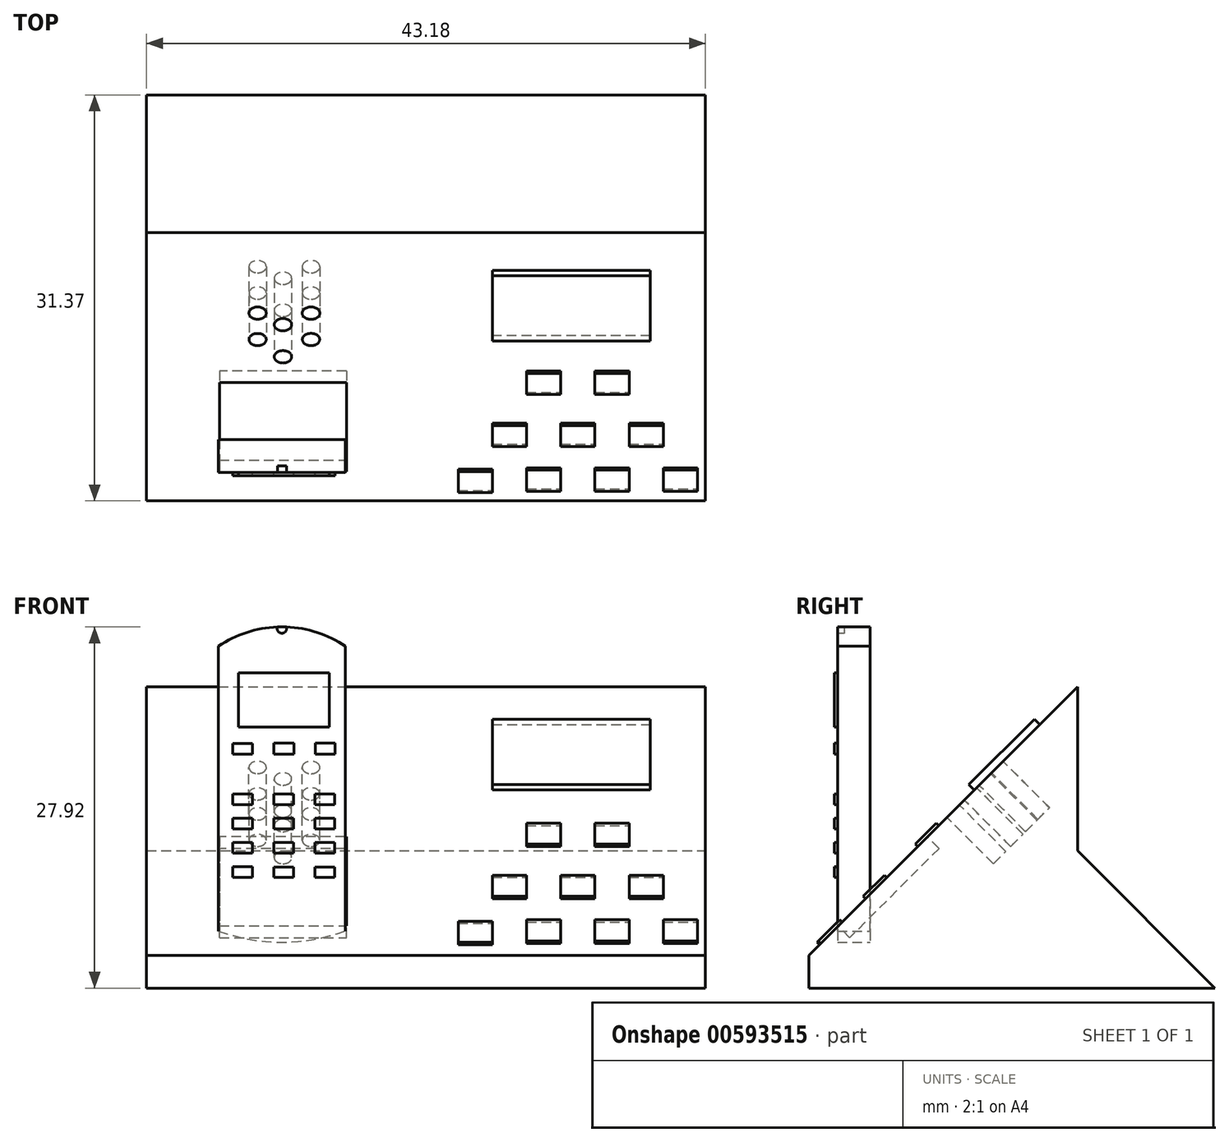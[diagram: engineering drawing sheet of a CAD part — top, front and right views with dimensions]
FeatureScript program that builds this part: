
annotation { "Feature Type Name" : "Feature", "Feature Type Description" : "" }
export const myFeature = defineFeature(function(context is Context, id is Id, definition is map)
    precondition{}
    {
        {
            var Q0;
            Q0=qCreatedBy(makeId("Top.planeOp"),FACE);
            var sketch = newSketch(context, id + "F0", { "sketchPlane" : qUnion([Q0])});
            skLineSegment(sketch, "E0", {"start": v(-21.03, 15.25) * mm, "end": v(22.15, 15.25) * mm});
            skLineSegment(sketch, "E1", {"start": v(-21.03, 15.25) * mm, "end": v(-21.03, -16.12) * mm});
            skLineSegment(sketch, "E2", {"start": v(-21.03, -16.12) * mm, "end": v(22.15, -16.12) * mm});
            skLineSegment(sketch, "E3", {"start": v(22.15, -16.12) * mm, "end": v(22.15, 15.25) * mm});
            skLineSegment(sketch, "E4", {"start": v(-21.03, 4.62) * mm, "end": v(22.15, 4.62) * mm});
            skSolve(sketch);
        }
        {
            var Q0;
            {var subQ0=sQuery(id+"F0.wireOp",EDGE,"E2");Q0=makeQuery(id+"F0.imprint","IMPRINT",FACE,{"disambiguationData":[TD([[makeQuery(id+"F0.imprint","IMPRINT",EDGE,{"derivedFrom":subQ0}),1.0]])]});}
            extrude(context, id + "F1", {"entities" : qUnion([Q0]), "depth" : 25.4 * mm, "offsetDistance" : 25.4 * mm});
        }
        {
            var Q0;
            {var subQ0=sQuery(id+"F0.wireOp",EDGE,"E0");Q0=makeQuery(id+"F0.imprint","IMPRINT",FACE,{"disambiguationData":[TD([[makeQuery(id+"F0.imprint","IMPRINT",EDGE,{"derivedFrom":subQ0}),-1.0]])]});}
            extrude(context, id + "F2", {"entities" : qUnion([Q0]), "operationType" : NewBodyOperationType.ADD, "depth" : 12.7 * mm, "offsetDistance" : 25.4 * mm});
        }
        {
            var Q0;
            Q0=makeQuery(id+"F1.opExtrude","CAP_EDGE",EDGE,{"disambiguationData":[OSD([sQuery(id+"F0.wireOp",EDGE,"E2")])],"isStart":false});
            chamfer(context, id + "F3", {"entities" : qUnion([Q0]), "width" : 22.86 * mm, "tangentPropagation" : true});
        }
        {
            var Q0;
            Q0=makeQuery(id+"F2.opExtrude","CAP_EDGE",EDGE,{"disambiguationData":[OSD([sQuery(id+"F0.wireOp",EDGE,"E0")])],"isStart":false});
            chamfer(context, id + "F4", {"entities" : qUnion([Q0]), "width" : 12.7 * mm, "tangentPropagation" : true});
        }
        {
            var Q0;
            Q0=makeQuery(id+"F3.opChamfer","BLEND_FACE",FACE,{"disambiguationData":[OSD([sQuery(id+"F0.wireOp",EDGE,"E2")])]});
            var sketch = newSketch(context, id + "F5", { "sketchPlane" : qUnion([Q0])});
            skLineSegment(sketch, "E5", {"start": v(-15.4, -6.41) * mm, "end": v(-5.59, -6.41) * mm});
            skLineSegment(sketch, "E6", {"start": v(-5.59, 3.34) * mm, "end": v(-15.4, 3.34) * mm});
            skLineSegment(sketch, "E7", {"start": v(-15.4, 3.34) * mm, "end": v(-15.4, -6.41) * mm});
            skLineSegment(sketch, "E8", {"start": v(-5.59, 3.34) * mm, "end": v(-5.59, -6.41) * mm});
            skSolve(sketch);
        }
        {
            var Q0;
            Q0=makeQuery(id+"F5.imprint","IMPRINT",FACE,{"disambiguationData":[TD([[makeQuery(id+"F5.imprint","IMPRINT",EDGE,{"derivedFrom":sQuery(id+"F5.wireOp",EDGE,"E5")}),1.0]])]});
            var Q1;
            {var subQ0=sQuery(id+"F5.wireOp",EDGE,"CrR3xn1p-6xJD-kxk5-ltNI-Yj6EOk7hMHrn");Q1=makeQuery(id+"F5.imprint","IMPRINT",FACE,{"disambiguationData":[TD([[makeQuery(id+"F5.imprint","IMPRINT",EDGE,{"derivedFrom":subQ0}),1.0]])]});}
            extrude(context, id + "F6", {"entities" : qUnion([Q0, Q1]), "operationType" : NewBodyOperationType.REMOVE, "oppositeDirection" : true, "depth" : 1.27 * mm, "offsetDistance" : 25.4 * mm});
        }
        {
            var Q0;
            {var subQ5=sQuery(id+"F5.wireOp",EDGE,"E5");Q0=makeQuery(id+"F5.imprint","IMPRINT",FACE,{"disambiguationData":[TD([[makeQuery(id+"F5.imprint","IMPRINT",EDGE,{"derivedFrom":subQ5}),-1.0]])]});}
            var sketch = newSketch(context, id + "F7", { "sketchPlane" : qUnion([Q0])});
            skLineSegment(sketch, "E9", {"start": v(5.69, 15.6) * mm, "end": v(17.9, 15.6) * mm});
            skLineSegment(sketch, "E10", {"start": v(17.9, 15.6) * mm, "end": v(17.9, 8.46) * mm});
            skLineSegment(sketch, "E11", {"start": v(17.9, 8.46) * mm, "end": v(5.69, 8.46) * mm});
            skLineSegment(sketch, "E12", {"start": v(5.69, 8.46) * mm, "end": v(5.69, 15.6) * mm});
            skLineSegment(sketch, "E13.bottom", {"start": v(8.32, 4.58) * mm, "end": v(10.97, 4.58) * mm});
            skLineSegment(sketch, "E13.top", {"start": v(8.32, 2.27) * mm, "end": v(10.97, 2.27) * mm});
            skLineSegment(sketch, "E13.left", {"start": v(8.32, 4.58) * mm, "end": v(8.32, 2.27) * mm});
            skLineSegment(sketch, "E13.right", {"start": v(10.97, 4.58) * mm, "end": v(10.97, 2.27) * mm});
            skLineSegment(sketch, "E14.bottom", {"start": v(13.61, 4.58) * mm, "end": v(16.25, 4.58) * mm});
            skLineSegment(sketch, "E14.top", {"start": v(13.61, 2.27) * mm, "end": v(16.25, 2.27) * mm});
            skLineSegment(sketch, "E14.left", {"start": v(13.61, 4.58) * mm, "end": v(13.61, 2.27) * mm});
            skLineSegment(sketch, "E14.right", {"start": v(16.25, 4.58) * mm, "end": v(16.25, 2.27) * mm});
            skLineSegment(sketch, "E15.bottom", {"start": v(5.69, -1.1) * mm, "end": v(8.33, -1.1) * mm});
            skLineSegment(sketch, "E15.top", {"start": v(5.69, -3.41) * mm, "end": v(8.33, -3.41) * mm});
            skLineSegment(sketch, "E15.left", {"start": v(5.69, -1.1) * mm, "end": v(5.69, -3.41) * mm});
            skLineSegment(sketch, "E15.right", {"start": v(8.33, -1.1) * mm, "end": v(8.33, -3.41) * mm});
            skLineSegment(sketch, "E16.bottom", {"start": v(10.97, -3.41) * mm, "end": v(13.61, -3.41) * mm});
            skLineSegment(sketch, "E16.top", {"start": v(10.97, -1.1) * mm, "end": v(13.61, -1.1) * mm});
            skLineSegment(sketch, "E16.left", {"start": v(10.97, -3.41) * mm, "end": v(10.97, -1.1) * mm});
            skLineSegment(sketch, "E16.right", {"start": v(13.61, -3.41) * mm, "end": v(13.61, -1.1) * mm});
            skLineSegment(sketch, "E17.bottom", {"start": v(16.25, -1.1) * mm, "end": v(18.9, -1.1) * mm});
            skLineSegment(sketch, "E17.top", {"start": v(16.25, -3.41) * mm, "end": v(18.9, -3.41) * mm});
            skLineSegment(sketch, "E17.left", {"start": v(16.25, -1.1) * mm, "end": v(16.25, -3.41) * mm});
            skLineSegment(sketch, "E17.right", {"start": v(18.9, -1.1) * mm, "end": v(18.9, -3.41) * mm});
            skPoint(sketch, "E18.oppositeSnap0", {"position": v(5.69, -2.26) * mm});
            skLineSegment(sketch, "E18.bottom", {"start": v(3.04, -6.14) * mm, "end": v(5.69, -6.14) * mm});
            skLineSegment(sketch, "E18.top", {"start": v(3.04, -8.45) * mm, "end": v(5.69, -8.45) * mm});
            skLineSegment(sketch, "E18.left", {"start": v(3.04, -6.14) * mm, "end": v(3.04, -8.45) * mm});
            skLineSegment(sketch, "E18.right", {"start": v(5.69, -6.14) * mm, "end": v(5.69, -8.45) * mm});
            skLineSegment(sketch, "E19.bottom", {"start": v(8.33, -6) * mm, "end": v(10.97, -6) * mm});
            skLineSegment(sketch, "E19.top", {"start": v(8.33, -8.3) * mm, "end": v(10.97, -8.3) * mm});
            skLineSegment(sketch, "E19.left", {"start": v(8.33, -6) * mm, "end": v(8.33, -8.3) * mm});
            skLineSegment(sketch, "E19.right", {"start": v(10.97, -6) * mm, "end": v(10.97, -8.3) * mm});
            skLineSegment(sketch, "E20", {"start": v(13.61, -8.3) * mm, "end": v(13.61, -6) * mm});
            skLineSegment(sketch, "E21", {"start": v(13.61, -6) * mm, "end": v(16.25, -6) * mm});
            skLineSegment(sketch, "E22", {"start": v(13.61, -8.3) * mm, "end": v(16.25, -8.3) * mm});
            skLineSegment(sketch, "E23", {"start": v(16.25, -8.3) * mm, "end": v(16.25, -6) * mm});
            skLineSegment(sketch, "E24", {"start": v(18.9, -8.3) * mm, "end": v(18.9, -6) * mm});
            skLineSegment(sketch, "E25", {"start": v(18.9, -6) * mm, "end": v(21.54, -6) * mm});
            skLineSegment(sketch, "E26", {"start": v(18.9, -8.3) * mm, "end": v(21.54, -8.3) * mm});
            skLineSegment(sketch, "E27", {"start": v(21.54, -8.3) * mm, "end": v(21.54, -6) * mm});
            skSolve(sketch);
        }
        {
            var Q0;
            Q0=makeQuery(id+"F7.imprint","IMPRINT",FACE,{"disambiguationData":[TD([[makeQuery(id+"F7.imprint","IMPRINT",EDGE,{"derivedFrom":sQuery(id+"F7.wireOp",EDGE,"E13.bottom")}),-1.0]])]});
            var Q1;
            Q1=makeQuery(id+"F7.imprint","IMPRINT",FACE,{"disambiguationData":[TD([[makeQuery(id+"F7.imprint","IMPRINT",EDGE,{"derivedFrom":sQuery(id+"F7.wireOp",EDGE,"E14.bottom")}),-1.0]])]});
            var Q2;
            Q2=makeQuery(id+"F7.imprint","IMPRINT",FACE,{"disambiguationData":[TD([[makeQuery(id+"F7.imprint","IMPRINT",EDGE,{"derivedFrom":sQuery(id+"F7.wireOp",EDGE,"E15.bottom")}),-1.0]])]});
            var Q3;
            Q3=makeQuery(id+"F7.imprint","IMPRINT",FACE,{"disambiguationData":[TD([[makeQuery(id+"F7.imprint","IMPRINT",EDGE,{"derivedFrom":sQuery(id+"F7.wireOp",EDGE,"E16.bottom")}),1.0]])]});
            var Q4;
            Q4=makeQuery(id+"F7.imprint","IMPRINT",FACE,{"disambiguationData":[TD([[makeQuery(id+"F7.imprint","IMPRINT",EDGE,{"derivedFrom":sQuery(id+"F7.wireOp",EDGE,"E17.bottom")}),-1.0]])]});
            var Q5;
            Q5=makeQuery(id+"F7.imprint","IMPRINT",FACE,{"disambiguationData":[TD([[makeQuery(id+"F7.imprint","IMPRINT",EDGE,{"derivedFrom":sQuery(id+"F7.wireOp",EDGE,"E18.bottom")}),-1.0]])]});
            var Q6;
            Q6=makeQuery(id+"F7.imprint","IMPRINT",FACE,{"disambiguationData":[TD([[makeQuery(id+"F7.imprint","IMPRINT",EDGE,{"derivedFrom":sQuery(id+"F7.wireOp",EDGE,"E19.bottom")}),-1.0]])]});
            var Q7;
            Q7=makeQuery(id+"F7.imprint","IMPRINT",FACE,{"disambiguationData":[TD([[makeQuery(id+"F7.imprint","IMPRINT",EDGE,{"derivedFrom":sQuery(id+"F7.wireOp",EDGE,"n9DK5ZvR-02UD-aitn-EGnA-fwqdZmRXGBVk.bottom")}),-1.0]])]});
            var Q8;
            Q8=makeQuery(id+"F7.imprint","IMPRINT",FACE,{"disambiguationData":[TD([[makeQuery(id+"F7.imprint","IMPRINT",EDGE,{"derivedFrom":sQuery(id+"F7.wireOp",EDGE,"2ktXjHqj-TVGW-xtYU-XM9Q-utSsLYBZR9na.bottom")}),-1.0]])]});
            var Q9;
            Q9=makeQuery(id+"F7.imprint","IMPRINT",FACE,{"disambiguationData":[TD([[makeQuery(id+"F7.imprint","IMPRINT",EDGE,{"derivedFrom":sQuery(id+"F7.wireOp",EDGE,"E20")}),-1.0]])]});
            var Q10;
            Q10=makeQuery(id+"F7.imprint","IMPRINT",FACE,{"disambiguationData":[TD([[makeQuery(id+"F7.imprint","IMPRINT",EDGE,{"derivedFrom":sQuery(id+"F7.wireOp",EDGE,"E24")}),-1.0]])]});
            extrude(context, id + "F8", {"entities" : qUnion([Q0, Q1, Q2, Q3, Q4, Q5, Q6, Q7, Q8, Q9, Q10]), "operationType" : NewBodyOperationType.ADD, "depth" : 0.25 * mm, "offsetDistance" : 25.4 * mm});
        }
        {
            var Q0;
            Q0=makeQuery(id+"F7.imprint","IMPRINT",FACE,{"disambiguationData":[TD([[makeQuery(id+"F7.imprint","IMPRINT",EDGE,{"derivedFrom":sQuery(id+"F7.wireOp",EDGE,"E9")}),-1.0]])]});
            extrude(context, id + "F9", {"entities" : qUnion([Q0]), "operationType" : NewBodyOperationType.ADD, "depth" : 0.58 * mm, "offsetDistance" : 25.4 * mm});
        }
        {
            var Q0;
            Q0=qCreatedBy(makeId("Front.planeOp"),FACE);
            var sketch = newSketch(context, id + "F10", { "sketchPlane" : qUnion([Q0])});
            skLineSegment(sketch, "E28", {"start": v(40.13, 22.63) * mm, "end": v(40.13, 0.6) * mm});
            skLineSegment(sketch, "E29", {"start": v(49.93, 0.6) * mm, "end": v(49.93, 22.63) * mm});
            skArc(sketch, "E30", {"start": v(49.93, 22.63) * mm, "mid": v(45.03, 24.11) * mm, "end": v(40.13, 22.63) * mm});
            skArc(sketch, "E31", {"start": v(40.13, 0.6) * mm, "mid": v(45.03, -0.26) * mm, "end": v(49.93, 0.6) * mm});
            skSolve(sketch);
        }
        {
            var Q0;
            Q0=makeQuery(id+"F10.imprint","IMPRINT",FACE,{"disambiguationData":[TD([[makeQuery(id+"F10.imprint","IMPRINT",EDGE,{"derivedFrom":sQuery(id+"F10.wireOp",EDGE,"E28")}),1.0]])]});
            extrude(context, id + "F11", {"entities" : qUnion([Q0]), "depth" : 2.54 * mm, "offsetDistance" : 25.4 * mm});
        }
        {
            var Q0;
            Q0=makeQuery(id+"F11.opExtrude","SWEPT_BODY",BODY,{"disambiguationData":[OSD([sQuery(id+"F10.wireOp",EDGE,"E28"),sQuery(id+"F10.wireOp",EDGE,"E29"),sQuery(id+"F10.wireOp",EDGE,"E30"),sQuery(id+"F10.wireOp",EDGE,"E31")])]});
            transform(context, id + "F12", {"entities" : qUnion([Q0]), "transformType" : TransformType.TRANSLATION_3D, "dx" : -55.6 * mm, "dy" : -11.38 * mm, "dz" : 3.81 * mm, "makeCopy" : false});
        }
        {
            var Q0;
            Q0=makeQuery(id+"F11.opExtrude","CAP_FACE",FACE,{"disambiguationData":[OSD([sQuery(id+"F10.wireOp",EDGE,"E28"),sQuery(id+"F10.wireOp",EDGE,"E29"),sQuery(id+"F10.wireOp",EDGE,"E30"),sQuery(id+"F10.wireOp",EDGE,"E31")])],"isStart":false});
            var sketch = newSketch(context, id + "F13", { "sketchPlane" : qUnion([Q0])});
            skPoint(sketch, "E32.cCircle.centerSnap0", {"position": v(-10.57, 27.92) * mm});
            skCircle(sketch, "E33", {"center": v(-10.57, 27.8) * mm, "radius": 0.37 * mm});
            skLineSegment(sketch, "E34.bottom", {"start": v(-13.94, 24.36) * mm, "end": v(-6.9, 24.36) * mm});
            skLineSegment(sketch, "E34.top", {"start": v(-13.94, 20.19) * mm, "end": v(-6.9, 20.19) * mm});
            skLineSegment(sketch, "E34.left", {"start": v(-13.94, 24.36) * mm, "end": v(-13.94, 20.19) * mm});
            skLineSegment(sketch, "E34.right", {"start": v(-6.9, 24.36) * mm, "end": v(-6.9, 20.19) * mm});
            skPoint(sketch, "E35.centerSnap0", {"position": v(-10.42, 20.19) * mm});
            skLineSegment(sketch, "E36.bottom", {"start": v(-14.36, 18.9) * mm, "end": v(-12.83, 18.9) * mm});
            skLineSegment(sketch, "E36.top", {"start": v(-14.36, 18.1) * mm, "end": v(-12.83, 18.1) * mm});
            skLineSegment(sketch, "E36.left", {"start": v(-14.36, 18.9) * mm, "end": v(-14.36, 18.1) * mm});
            skLineSegment(sketch, "E36.right", {"start": v(-12.83, 18.9) * mm, "end": v(-12.83, 18.1) * mm});
            skLineSegment(sketch, "E37.bottom", {"start": v(-11.18, 18.93) * mm, "end": v(-9.65, 18.93) * mm});
            skLineSegment(sketch, "E37.top", {"start": v(-11.18, 18.1) * mm, "end": v(-9.65, 18.1) * mm});
            skLineSegment(sketch, "E37.left", {"start": v(-11.18, 18.93) * mm, "end": v(-11.18, 18.1) * mm});
            skLineSegment(sketch, "E37.right", {"start": v(-9.65, 18.93) * mm, "end": v(-9.65, 18.1) * mm});
            skLineSegment(sketch, "E38.bottom", {"start": v(-8, 18.93) * mm, "end": v(-6.48, 18.93) * mm});
            skLineSegment(sketch, "E38.top", {"start": v(-8, 18.1) * mm, "end": v(-6.48, 18.1) * mm});
            skLineSegment(sketch, "E38.left", {"start": v(-8, 18.93) * mm, "end": v(-8, 18.1) * mm});
            skLineSegment(sketch, "E38.right", {"start": v(-6.48, 18.93) * mm, "end": v(-6.48, 18.1) * mm});
            skCircle(sketch, "E39", {"center": v(-10.42, 16.7) * mm, "radius": 0.91 * mm});
            skLineSegment(sketch, "E40.bottom", {"start": v(-14.36, 15) * mm, "end": v(-12.84, 15) * mm});
            skLineSegment(sketch, "E40.top", {"start": v(-14.36, 14.2) * mm, "end": v(-12.84, 14.2) * mm});
            skLineSegment(sketch, "E40.left", {"start": v(-14.36, 15) * mm, "end": v(-14.36, 14.2) * mm});
            skLineSegment(sketch, "E40.right", {"start": v(-12.84, 15) * mm, "end": v(-12.84, 14.2) * mm});
            skLineSegment(sketch, "E41.bottom", {"start": v(-11.18, 15) * mm, "end": v(-9.66, 15) * mm});
            skLineSegment(sketch, "E41.top", {"start": v(-11.18, 14.2) * mm, "end": v(-9.66, 14.2) * mm});
            skLineSegment(sketch, "E41.left", {"start": v(-11.18, 15) * mm, "end": v(-11.18, 14.2) * mm});
            skLineSegment(sketch, "E41.right", {"start": v(-9.66, 15) * mm, "end": v(-9.66, 14.2) * mm});
            skLineSegment(sketch, "E42.bottom", {"start": v(-8, 15) * mm, "end": v(-6.49, 15) * mm});
            skLineSegment(sketch, "E42.top", {"start": v(-8, 14.2) * mm, "end": v(-6.49, 14.2) * mm});
            skLineSegment(sketch, "E42.left", {"start": v(-8, 15) * mm, "end": v(-8, 14.2) * mm});
            skLineSegment(sketch, "E42.right", {"start": v(-6.49, 15) * mm, "end": v(-6.49, 14.2) * mm});
            skLineSegment(sketch, "E43.bottom", {"start": v(-14.36, 13.13) * mm, "end": v(-12.84, 13.13) * mm});
            skLineSegment(sketch, "E43.top", {"start": v(-14.36, 12.32) * mm, "end": v(-12.84, 12.32) * mm});
            skLineSegment(sketch, "E43.left", {"start": v(-14.36, 13.13) * mm, "end": v(-14.36, 12.32) * mm});
            skLineSegment(sketch, "E43.right", {"start": v(-12.84, 13.13) * mm, "end": v(-12.84, 12.32) * mm});
            skLineSegment(sketch, "E44.bottom", {"start": v(-14.36, 11.25) * mm, "end": v(-12.84, 11.25) * mm});
            skLineSegment(sketch, "E44.top", {"start": v(-14.36, 10.44) * mm, "end": v(-12.84, 10.44) * mm});
            skLineSegment(sketch, "E44.left", {"start": v(-14.36, 11.25) * mm, "end": v(-14.36, 10.44) * mm});
            skLineSegment(sketch, "E44.right", {"start": v(-12.84, 11.25) * mm, "end": v(-12.84, 10.44) * mm});
            skLineSegment(sketch, "E45.bottom", {"start": v(-14.36, 9.37) * mm, "end": v(-12.84, 9.37) * mm});
            skLineSegment(sketch, "E45.top", {"start": v(-14.36, 8.56) * mm, "end": v(-12.84, 8.56) * mm});
            skLineSegment(sketch, "E45.left", {"start": v(-14.36, 9.37) * mm, "end": v(-14.36, 8.56) * mm});
            skLineSegment(sketch, "E45.right", {"start": v(-12.84, 9.37) * mm, "end": v(-12.84, 8.56) * mm});
            skLineSegment(sketch, "E46.bottom", {"start": v(-11.18, 13.12) * mm, "end": v(-9.66, 13.12) * mm});
            skLineSegment(sketch, "E46.top", {"start": v(-11.18, 12.32) * mm, "end": v(-9.66, 12.32) * mm});
            skLineSegment(sketch, "E46.left", {"start": v(-11.18, 13.12) * mm, "end": v(-11.18, 12.32) * mm});
            skLineSegment(sketch, "E46.right", {"start": v(-9.66, 13.12) * mm, "end": v(-9.66, 12.32) * mm});
            skLineSegment(sketch, "E47.bottom", {"start": v(-8, 13.12) * mm, "end": v(-6.49, 13.12) * mm});
            skLineSegment(sketch, "E47.top", {"start": v(-8, 12.31) * mm, "end": v(-6.49, 12.31) * mm});
            skLineSegment(sketch, "E47.left", {"start": v(-8, 13.12) * mm, "end": v(-8, 12.31) * mm});
            skLineSegment(sketch, "E47.right", {"start": v(-6.49, 13.12) * mm, "end": v(-6.49, 12.31) * mm});
            skLineSegment(sketch, "E48.bottom", {"start": v(-11.18, 11.25) * mm, "end": v(-9.66, 11.25) * mm});
            skLineSegment(sketch, "E48.top", {"start": v(-11.18, 10.43) * mm, "end": v(-9.66, 10.43) * mm});
            skLineSegment(sketch, "E48.left", {"start": v(-11.18, 11.25) * mm, "end": v(-11.18, 10.43) * mm});
            skLineSegment(sketch, "E48.right", {"start": v(-9.66, 11.25) * mm, "end": v(-9.66, 10.43) * mm});
            skLineSegment(sketch, "E49.bottom", {"start": v(-8, 11.24) * mm, "end": v(-6.49, 11.24) * mm});
            skLineSegment(sketch, "E49.top", {"start": v(-8, 10.43) * mm, "end": v(-6.49, 10.43) * mm});
            skLineSegment(sketch, "E49.left", {"start": v(-8, 11.24) * mm, "end": v(-8, 10.43) * mm});
            skLineSegment(sketch, "E49.right", {"start": v(-6.49, 11.24) * mm, "end": v(-6.49, 10.43) * mm});
            skLineSegment(sketch, "E50.bottom", {"start": v(-11.18, 9.36) * mm, "end": v(-9.66, 9.36) * mm});
            skLineSegment(sketch, "E50.top", {"start": v(-11.18, 8.55) * mm, "end": v(-9.66, 8.55) * mm});
            skLineSegment(sketch, "E50.left", {"start": v(-11.18, 9.36) * mm, "end": v(-11.18, 8.55) * mm});
            skLineSegment(sketch, "E50.right", {"start": v(-9.66, 9.36) * mm, "end": v(-9.66, 8.55) * mm});
            skLineSegment(sketch, "E51.bottom", {"start": v(-8, 9.36) * mm, "end": v(-6.49, 9.36) * mm});
            skLineSegment(sketch, "E51.top", {"start": v(-8, 8.57) * mm, "end": v(-6.49, 8.57) * mm});
            skLineSegment(sketch, "E51.left", {"start": v(-8, 9.36) * mm, "end": v(-8, 8.57) * mm});
            skLineSegment(sketch, "E51.right", {"start": v(-6.49, 9.36) * mm, "end": v(-6.49, 8.57) * mm});
            skSolve(sketch);
        }
        {
            var Q0;
            Q0=makeQuery(id+"F13.imprint","IMPRINT",FACE,{"disambiguationData":[TD([[makeQuery(id+"F13.imprint","IMPRINT",EDGE,{"derivedFrom":sQuery(id+"F13.wireOp",EDGE,"E40.bottom")}),-1.0]])]});
            var Q1;
            Q1=makeQuery(id+"F13.imprint","IMPRINT",FACE,{"disambiguationData":[TD([[makeQuery(id+"F13.imprint","IMPRINT",EDGE,{"derivedFrom":sQuery(id+"F13.wireOp",EDGE,"E41.bottom")}),-1.0]])]});
            var Q2;
            Q2=makeQuery(id+"F13.imprint","IMPRINT",FACE,{"disambiguationData":[TD([[makeQuery(id+"F13.imprint","IMPRINT",EDGE,{"derivedFrom":sQuery(id+"F13.wireOp",EDGE,"E43.bottom")}),-1.0]])]});
            var Q3;
            Q3=makeQuery(id+"F13.imprint","IMPRINT",FACE,{"disambiguationData":[TD([[makeQuery(id+"F13.imprint","IMPRINT",EDGE,{"derivedFrom":sQuery(id+"F13.wireOp",EDGE,"E46.bottom")}),-1.0]])]});
            var Q4;
            Q4=makeQuery(id+"F13.imprint","IMPRINT",FACE,{"disambiguationData":[TD([[makeQuery(id+"F13.imprint","IMPRINT",EDGE,{"derivedFrom":sQuery(id+"F13.wireOp",EDGE,"E47.bottom")}),-1.0]])]});
            var Q5;
            Q5=makeQuery(id+"F13.imprint","IMPRINT",FACE,{"disambiguationData":[TD([[makeQuery(id+"F13.imprint","IMPRINT",EDGE,{"derivedFrom":sQuery(id+"F13.wireOp",EDGE,"E42.bottom")}),-1.0]])]});
            var Q6;
            Q6=makeQuery(id+"F13.imprint","IMPRINT",FACE,{"disambiguationData":[TD([[makeQuery(id+"F13.imprint","IMPRINT",EDGE,{"derivedFrom":sQuery(id+"F13.wireOp",EDGE,"E48.bottom")}),-1.0]])]});
            var Q7;
            Q7=makeQuery(id+"F13.imprint","IMPRINT",FACE,{"disambiguationData":[TD([[makeQuery(id+"F13.imprint","IMPRINT",EDGE,{"derivedFrom":sQuery(id+"F13.wireOp",EDGE,"E49.bottom")}),-1.0]])]});
            var Q8;
            Q8=makeQuery(id+"F13.imprint","IMPRINT",FACE,{"disambiguationData":[TD([[makeQuery(id+"F13.imprint","IMPRINT",EDGE,{"derivedFrom":sQuery(id+"F13.wireOp",EDGE,"E51.bottom")}),-1.0]])]});
            var Q9;
            Q9=makeQuery(id+"F13.imprint","IMPRINT",FACE,{"disambiguationData":[TD([[makeQuery(id+"F13.imprint","IMPRINT",EDGE,{"derivedFrom":sQuery(id+"F13.wireOp",EDGE,"E50.bottom")}),-1.0]])]});
            var Q10;
            Q10=makeQuery(id+"F13.imprint","IMPRINT",FACE,{"disambiguationData":[TD([[makeQuery(id+"F13.imprint","IMPRINT",EDGE,{"derivedFrom":sQuery(id+"F13.wireOp",EDGE,"E45.bottom")}),-1.0]])]});
            var Q11;
            Q11=makeQuery(id+"F13.imprint","IMPRINT",FACE,{"disambiguationData":[TD([[makeQuery(id+"F13.imprint","IMPRINT",EDGE,{"derivedFrom":sQuery(id+"F13.wireOp",EDGE,"E44.bottom")}),-1.0]])]});
            var Q12;
            Q12=makeQuery(id+"F13.imprint","IMPRINT",FACE,{"disambiguationData":[TD([[makeQuery(id+"F13.imprint","IMPRINT",EDGE,{"derivedFrom":sQuery(id+"F13.wireOp",EDGE,"E36.bottom")}),-1.0]])]});
            var Q13;
            Q13=makeQuery(id+"F13.imprint","IMPRINT",FACE,{"disambiguationData":[TD([[makeQuery(id+"F13.imprint","IMPRINT",EDGE,{"derivedFrom":sQuery(id+"F13.wireOp",EDGE,"E37.bottom")}),-1.0]])]});
            var Q14;
            Q14=makeQuery(id+"F13.imprint","IMPRINT",FACE,{"disambiguationData":[TD([[makeQuery(id+"F13.imprint","IMPRINT",EDGE,{"derivedFrom":sQuery(id+"F13.wireOp",EDGE,"E38.bottom")}),-1.0]])]});
            var Q15;
            Q15=makeQuery(id+"F13.imprint","IMPRINT",FACE,{"disambiguationData":[TD([[makeQuery(id+"F13.imprint","IMPRINT",EDGE,{"derivedFrom":sQuery(id+"F13.wireOp",EDGE,"E34.bottom")}),-1.0]])]});
            extrude(context, id + "F14", {"entities" : qUnion([Q0, Q1, Q2, Q3, Q4, Q5, Q6, Q7, Q8, Q9, Q10, Q11, Q12, Q13, Q14, Q15]), "operationType" : NewBodyOperationType.ADD, "depth" : 0.25 * mm, "offsetDistance" : 25.4 * mm});
        }
        {
            var Q0;
            Q0=makeQuery(id+"F13.imprint","IMPRINT",FACE,{"disambiguationData":[TD([[makeQuery(id+"F13.imprint","IMPRINT",EDGE,{"derivedFrom":sQuery(id+"F13.wireOp",EDGE,"E33")}),1.0]])]});
            extrude(context, id + "F15", {"entities" : qUnion([Q0]), "operationType" : NewBodyOperationType.REMOVE, "oppositeDirection" : true, "depth" : 0.5 * mm, "offsetDistance" : 25.4 * mm});
        }
        {
            var Q0;
            Q0=makeQuery(id+"F3.opChamfer","BLEND_FACE",FACE,{"disambiguationData":[OSD([sQuery(id+"F0.wireOp",EDGE,"E2")])]});
            var sketch = newSketch(context, id + "F16", { "sketchPlane" : qUnion([Q0])});
            skCircle(sketch, "E52", {"center": v(-10.5, 9.66) * mm, "radius": 0.68 * mm});
            skPoint(sketch, "E52.centerSnap0", {"position": v(-10.5, 3.34) * mm});
            skCircle(sketch, "E53", {"center": v(-8.32, 8.04) * mm, "radius": 0.67 * mm});
            skCircle(sketch, "E54", {"center": v(-12.45, 8.04) * mm, "radius": 0.67 * mm});
            skCircle(sketch, "E55", {"center": v(-10.5, 6.15) * mm, "radius": 0.68 * mm});
            skCircle(sketch, "E56", {"center": v(-12.45, 10.93) * mm, "radius": 0.67 * mm});
            skCircle(sketch, "E57", {"center": v(-8.32, 10.93) * mm, "radius": 0.68 * mm});
            skSolve(sketch);
        }
        {
            var Q0;
            Q0=makeQuery(id+"F16.imprint","IMPRINT",FACE,{"disambiguationData":[TD([[makeQuery(id+"F16.imprint","IMPRINT",EDGE,{"derivedFrom":sQuery(id+"F16.wireOp",EDGE,"E52")}),1.0]])]});
            var Q1;
            Q1=makeQuery(id+"F16.imprint","IMPRINT",FACE,{"disambiguationData":[TD([[makeQuery(id+"F16.imprint","IMPRINT",EDGE,{"derivedFrom":sQuery(id+"F16.wireOp",EDGE,"E53")}),1.0]])]});
            var Q2;
            Q2=makeQuery(id+"F16.imprint","IMPRINT",FACE,{"disambiguationData":[TD([[makeQuery(id+"F16.imprint","IMPRINT",EDGE,{"derivedFrom":sQuery(id+"F16.wireOp",EDGE,"E54")}),1.0]])]});
            var Q3;
            Q3=makeQuery(id+"F16.imprint","IMPRINT",FACE,{"disambiguationData":[TD([[makeQuery(id+"F16.imprint","IMPRINT",EDGE,{"derivedFrom":sQuery(id+"F16.wireOp",EDGE,"E55")}),1.0]])]});
            var Q4;
            Q4=makeQuery(id+"F16.imprint","IMPRINT",FACE,{"disambiguationData":[TD([[makeQuery(id+"F16.imprint","IMPRINT",EDGE,{"derivedFrom":sQuery(id+"F16.wireOp",EDGE,"E57")}),1.0]])]});
            var Q5;
            Q5=makeQuery(id+"F16.imprint","IMPRINT",FACE,{"disambiguationData":[TD([[makeQuery(id+"F16.imprint","IMPRINT",EDGE,{"derivedFrom":sQuery(id+"F16.wireOp",EDGE,"E56")}),1.0]])]});
            extrude(context, id + "F17", {"entities" : qUnion([Q0, Q1, Q2, Q3, Q4, Q5]), "operationType" : NewBodyOperationType.REMOVE, "oppositeDirection" : true, "depth" : 5.08 * mm, "offsetDistance" : 25.4 * mm});
        }
    });
